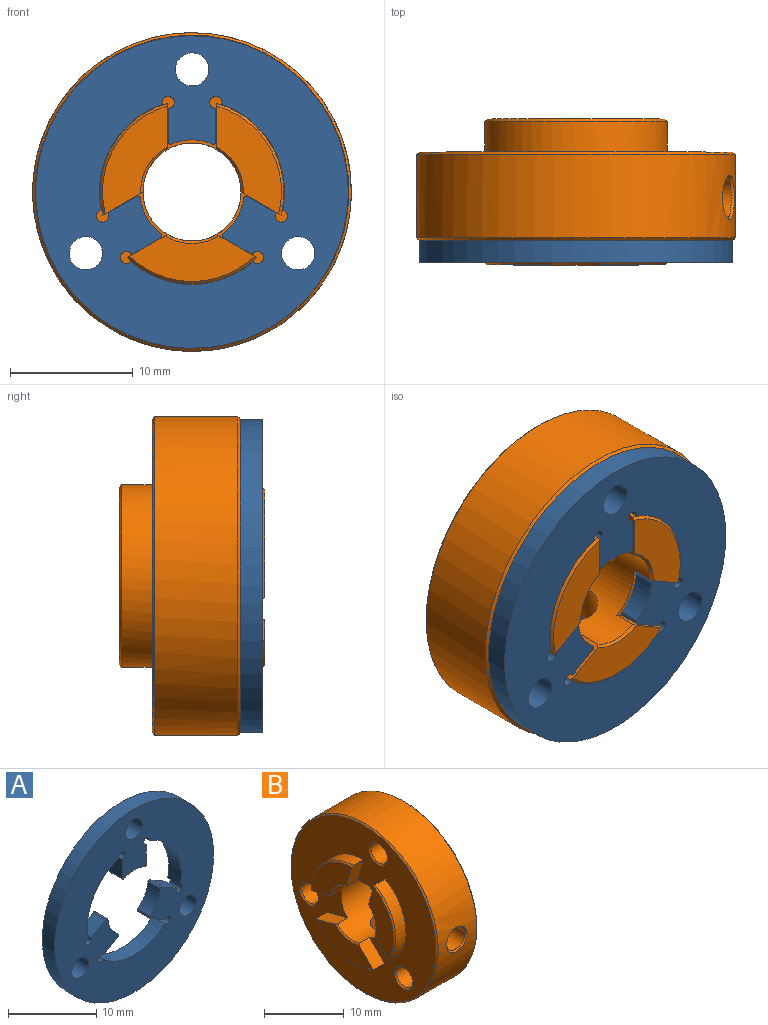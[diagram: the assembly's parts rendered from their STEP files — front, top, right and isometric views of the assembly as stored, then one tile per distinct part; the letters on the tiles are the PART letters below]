
ASSEMBLY  parts=2 mates=1
PART A: 30 faces, bbox 25.5x2x25.5 mm
  f0: cylinder r=7.55mm len=8.62mm, axis (0,1,0), area 21.7mm2, adj f16,f17,f24,f29
  f1: plane 2.7x2mm, normal (-1,0,0), area 5.4mm2, adj f16,f17,f23,f24
  f2: cylinder r=4.25mm len=3.34mm, axis (0,1,0), area 6.9mm2, adj f16,f17,f22,f23
  f3: plane 2.7x2mm, normal (1,0,0), area 5.4mm2, adj f16,f17,f22,f25
  f4: cylinder r=7.55mm len=8.62mm, axis (0,1,0), area 21.7mm2, adj f16,f17,f25,f26
  f5: plane 2.34x2mm, normal (0.5,0,0.87), area 5.4mm2, adj f16,f17,f20,f26
  f6: cylinder r=4.25mm len=2.9mm, axis (0,1,0), area 6.9mm2, adj f16,f17,f20,f21
  f7: plane 2.34x2mm, normal (-0.5,0,-0.87), area 5.4mm2, adj f16,f17,f21,f27
  f8: cylinder r=7.55mm len=9.95mm, axis (0,1,0), area 21.7mm2, adj f16,f17,f27,f28
  f9: plane 2.34x2mm, normal (0.5,0,-0.87), area 5.4mm2, adj f16,f17,f18,f28
  f10: cylinder r=4.25mm len=2.9mm, axis (0,1,0), area 6.9mm2, adj f16,f17,f18,f19
  f11: cylinder r=1.35mm len=2.7mm, axis (0,1,0), area 17mm2, adj f16,f17
  f12: cylinder r=1.35mm len=2.7mm, axis (0,1,0), area 17mm2, adj f16,f17
  f13: plane 2.34x2mm, normal (-0.5,0,0.87), area 5.4mm2, adj f16,f17,f19,f29
  f14: cylinder r=12.75mm len=25.5mm, axis (0,1,0), area 160.2mm2, adj f16,f17
  f15: cylinder r=1.35mm len=2.7mm, axis (0,1,0), area 17mm2, adj f16,f17
  f16: plane 25.5x25.5mm, normal (0,-1,0), area 350mm2, adj f0,f1,f2,f3,f4,f5,f6,f7
  f17: plane 25.5x25.5mm, normal (0,1,0), area 350mm2, adj f0,f1,f2,f3,f4,f5,f6,f7
  f18: cylinder r=0.2mm len=2mm, axis (0,1,0), area 0.8mm2, adj f9,f10,f16,f17
  f19: cylinder r=0.2mm len=2mm, axis (0,1,0), area 0.8mm2, adj f10,f13,f16,f17
  f20: cylinder r=0.2mm len=2mm, axis (0,1,0), area 0.8mm2, adj f5,f6,f16,f17
  f21: cylinder r=0.2mm len=2mm, axis (0,1,0), area 0.8mm2, adj f6,f7,f16,f17
  f22: cylinder r=0.2mm len=2mm, axis (0,1,0), area 0.8mm2, adj f2,f3,f16,f17
  f23: cylinder r=0.2mm len=2mm, axis (0,1,0), area 0.8mm2, adj f1,f2,f16,f17
  f24: cylinder r=0.5mm len=2mm, axis (0,-1,0), area 5mm2, adj f0,f1,f16,f17
  f25: cylinder r=0.5mm len=2mm, axis (0,-1,0), area 5mm2, adj f3,f4,f16,f17
  f26: cylinder r=0.5mm len=2mm, axis (0,-1,0), area 5mm2, adj f4,f5,f16,f17
  f27: cylinder r=0.5mm len=2mm, axis (0,-1,0), area 5mm2, adj f7,f8,f16,f17
  f28: cylinder r=0.5mm len=2mm, axis (0,-1,0), area 5mm2, adj f8,f9,f16,f17
  f29: cylinder r=0.5mm len=2mm, axis (0,-1,0), area 5mm2, adj f0,f13,f16,f17
PART B: 41 faces, bbox 11.9x26x26 mm
  f0: plane 7.18x7.18mm, normal (-1,0,0), area 24.6mm2, adj f20,f22,f26,f29
  f1: plane 9.81x4.41mm, normal (-1,0,0), area 24.6mm2, adj f18,f19,f27,f30
  f2: plane 9.81x4.41mm, normal (-1,0,0), area 24.6mm2, adj f17,f21,f28,f31
  f3: cylinder r=4mm len=11.5mm, axis (-1,0,0), area 249.4mm2, adj f14,f15,f16,f17,f18,f19,f20,f21
  f4: cylinder r=7.5mm len=10.16mm, axis (-1,0,0), area 21mm2, adj f16,f17,f21,f31
  f5: cylinder r=7.5mm len=7.44mm, axis (-1,0,0), area 21mm2, adj f16,f20,f22,f29
  f6: cylinder r=7.5mm len=10.16mm, axis (-1,0,0), area 21mm2, adj f16,f18,f19,f30
  f7: cylinder r=13mm len=26mm, axis (-1,0,0), area 534mm2, adj f32,f33,f34,f35
  f8: cylinder r=1.45mm len=6.8mm, axis (-1,0,0), area 62mm2, adj f25,f37
  f9: cylinder r=1.45mm len=6.8mm, axis (-1,0,0), area 62mm2, adj f23,f38
  f10: cylinder r=1.45mm len=6.8mm, axis (-1,0,0), area 62mm2, adj f24,f36
  f11: plane 14.5x14.5mm, normal (1,0,0), area 109.7mm2, adj f39,f40
  f12: cylinder r=7.45mm len=14.9mm, axis (-1,0,0), area 117mm2, adj f13,f39
  f13: plane 25.6x25.6mm, normal (1,0,0), area 314.7mm2, adj f12,f33,f36,f37,f38
  f14: cylinder r=1.62mm len=9.01mm, axis (0,1,0), area 92mm2, adj f3,f35
  f15: cylinder r=1.62mm len=8.8mm, axis (0,0,1), area 89.8mm2, adj f3,f34
  f16: plane 25.6x25.6mm, normal (-1,0,0), area 355.3mm2, adj f3,f4,f5,f6,f17,f18,f19,f20
  f17: plane 2.66x2.66mm, normal (0,0.71,-0.71), area 7.5mm2, adj f2,f3,f4,f16,f28,f31
  f18: plane 2.66x2.66mm, normal (0,-0.71,0.71), area 7.5mm2, adj f1,f3,f6,f16,f27,f30
  f19: plane 3.64x2mm, normal (0,0.26,0.97), area 7.5mm2, adj f1,f3,f6,f16,f27,f30
  f20: plane 3.64x2mm, normal (0,-0.26,-0.97), area 7.5mm2, adj f0,f3,f5,f16,f26,f29
  f21: plane 3.64x2mm, normal (0,0.97,0.26), area 7.5mm2, adj f2,f3,f4,f16,f28,f31
  f22: plane 3.64x2mm, normal (0,-0.97,-0.26), area 7.5mm2, adj f0,f3,f5,f16,f26,f29
  f23: cone r=1.65mm half-angle=45deg, axis (-1,0,0), area 2.8mm2, adj f9,f16
  f24: cone r=1.65mm half-angle=45deg, axis (-1,0,0), area 2.8mm2, adj f10,f16
  f25: cone r=1.65mm half-angle=45deg, axis (-1,0,0), area 2.8mm2, adj f8,f16
  f26: cone r=4mm half-angle=45deg, axis (-1,0,0), area 1.2mm2, adj f0,f3,f20,f22
  f27: cone r=4mm half-angle=45deg, axis (-1,0,0), area 1.2mm2, adj f1,f3,f18,f19
  f28: cone r=4mm half-angle=45deg, axis (-1,0,0), area 1.2mm2, adj f2,f3,f17,f21
  f29: cone r=7.3mm half-angle=45deg, axis (1,0,0), area 3.2mm2, adj f0,f5,f20,f22
  f30: cone r=7.3mm half-angle=45deg, axis (1,0,0), area 3.2mm2, adj f1,f6,f18,f19
  f31: cone r=7.3mm half-angle=45deg, axis (1,0,0), area 3.2mm2, adj f2,f4,f17,f21
  f32: cone r=13mm half-angle=45deg, axis (1,0,0), area 22.9mm2, adj f7,f16
  f33: cone r=13mm half-angle=45deg, axis (-1,0,0), area 22.9mm2, adj f7,f13
  f34: bspline ~3.71x3.65mm, area 3.2mm2, adj f7,f15
  f35: bspline ~3.7x3.65mm, area 3.2mm2, adj f7,f14
  f36: cone r=1.45mm half-angle=45deg, axis (1,0,0), area 2.8mm2, adj f10,f13
  f37: cone r=1.45mm half-angle=45deg, axis (1,0,0), area 2.8mm2, adj f8,f13
  f38: cone r=1.45mm half-angle=45deg, axis (1,0,0), area 2.8mm2, adj f9,f13
  f39: cone r=7.45mm half-angle=45deg, axis (-1,0,0), area 13.1mm2, adj f11,f12
  f40: cone r=4.2mm half-angle=45deg, axis (1,0,0), area 7.3mm2, adj f3,f11
PLACE A t=(5.92,-3.78,-0.01)mm
PLACE B rot(axis=(-0.13,-0.13,0.98),91deg) t=(5.92,-5.98,-0.01)mm
MATE revolute A.f0 <-> B.f3  axis (0,1,0) through (5.92,-3.78,-0.01)mm
